# Revit family: WC BOLMEN16_RFA
name_source: partatom
category: Aparatos sanitarios
units: mm (PartAtom-declared; Revit-internal decimal feet)

## family parameters
Compartido = Sí
Corte con vacíos al cargar = No
Cota de conector redondo = Diámetro de uso
Número OmniClass = 23.45.00.00
Punto de cálculo de habitación = No
Se basa en plano de trabajo = No
Siempre vertical = Sí
Tipo de pieza = Normal
Título OmniClass = Sanitary, Laundry, and Cleaning Equipment

## types (1)
- WC BOLMEN16
    Comentarios de tipo = SANIVEX
    Conexión AF = Sí
    Descripción = WC Taza Tanque Bolmen 16, 4.8 lpd, Color Blanco.
    Elevación por defecto = 0"
    Fabricante = HELVEX
    High Gloss Ceramic = High Gloss Ceramic
    Inlet Threads = A la alimentación Ø15/16 -14 NS-1. A la descarga se acopla al Ø de drenaje de 4"
con brida sanitaria o cuello de cera.
    Marfil = Marfil
    Max. Working Pressure = 85.3 psi
    Maximum Consumption = 1.25 gpf
    Min. Working Pressure = 3.6 psi
    Modelo = WC BOLMEN16
    Technical Details = Diseño ergonómico de construcción robusta
con cerámica de 10mm de espesor, con
sistema de descarga Turvex con sifón jet y
espejo de agua óptimo, mueble libre de
alabeo (base plana).
    Total Height = 33"
    Total Length = 30"
    Total Width = 15"
    Warranty = 5 Years Warranty In Iron Fittings

## geometry (parser evidence)
native form markers: Sweep x3
no freeform markers — native parametric forms only
